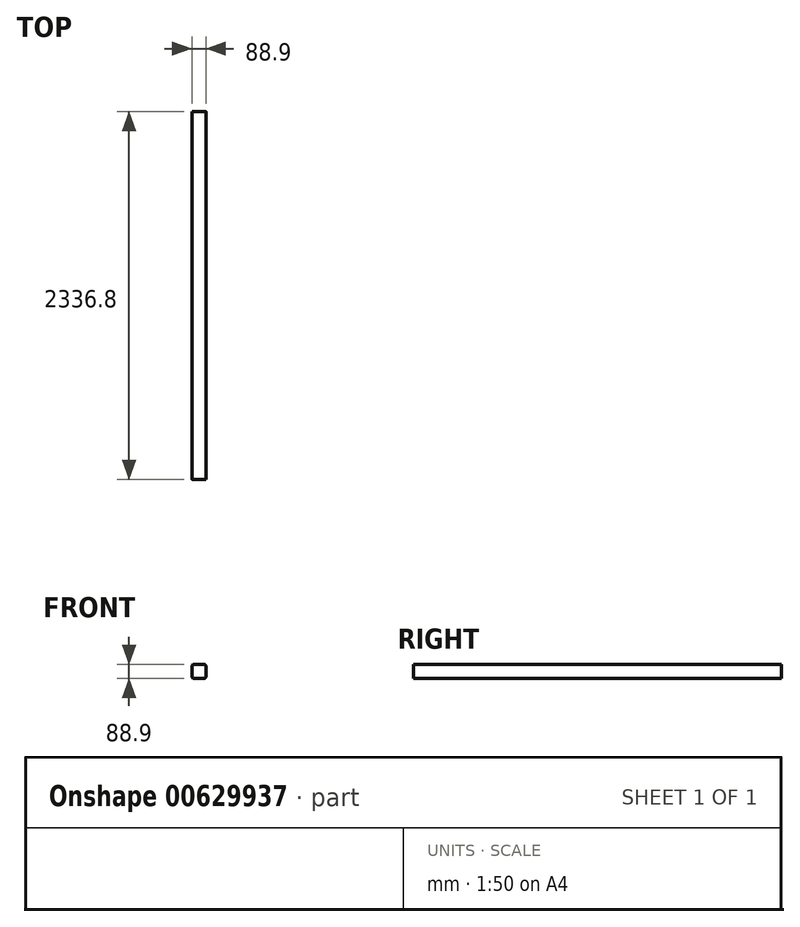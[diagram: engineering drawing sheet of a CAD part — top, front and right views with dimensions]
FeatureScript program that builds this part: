
annotation { "Feature Type Name" : "Feature", "Feature Type Description" : "" }
export const myFeature = defineFeature(function(context is Context, id is Id, definition is map)
    precondition{}
    {
        {
            var Q0;
            Q0=qCreatedBy(makeId("Front.planeOp"),FACE);
            var sketch = newSketch(context, id + "F0", { "sketchPlane" : qUnion([Q0])});
            skLineSegment(sketch, "E0.bottom", {"start": v(-35.1, 88.9) * mm, "end": v(28.4, 88.9) * mm});
            skLineSegment(sketch, "E0.top", {"start": v(-35.1, 0) * mm, "end": v(28.4, 0) * mm});
            skLineSegment(sketch, "E0.left", {"start": v(-47.8, 76.2) * mm, "end": v(-47.8, 12.7) * mm});
            skLineSegment(sketch, "E0.right", {"start": v(41.1, 76.2) * mm, "end": v(41.1, 12.7) * mm});
            skPoint(sketch, "E1.visualSharp", {"position": v(-47.8, 88.9) * mm});
            skArc(sketch, "E1.filletArc", {"start": v(-35.1, 88.9) * mm, "mid": v(-44.08, 85.18) * mm, "end": v(-47.8, 76.2) * mm});
            skPoint(sketch, "E2.visualSharp", {"position": v(41.1, 88.9) * mm});
            skArc(sketch, "E2.filletArc", {"start": v(41.1, 76.2) * mm, "mid": v(37.38, 85.18) * mm, "end": v(28.4, 88.9) * mm});
            skPoint(sketch, "E3.visualSharp", {"position": v(41.1, 0) * mm});
            skArc(sketch, "E3.filletArc", {"start": v(28.4, 0) * mm, "mid": v(37.38, 3.72) * mm, "end": v(41.1, 12.7) * mm});
            skPoint(sketch, "E4.visualSharp", {"position": v(-47.8, 0) * mm});
            skArc(sketch, "E4.filletArc", {"start": v(-47.8, 12.7) * mm, "mid": v(-44.08, 3.72) * mm, "end": v(-35.1, 0) * mm});
            skSolve(sketch);
        }
        {
            var Q0;
            Q0=makeQuery(id+"F0.imprint","IMPRINT",FACE,{"disambiguationData":[TD([[makeQuery(id+"F0.imprint","IMPRINT",EDGE,{"derivedFrom":sQuery(id+"F0.wireOp",EDGE,"E0.bottom")}),-1.0]])]});
            extrude(context, id + "F1", {"entities" : qUnion([Q0]), "depth" : 2336.8 * mm, "offsetDistance" : 25.4 * mm});
        }
    });
